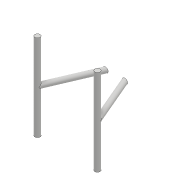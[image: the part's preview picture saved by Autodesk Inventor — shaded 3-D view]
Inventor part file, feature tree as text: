
AUTODESK INVENTOR PART (.ipt)
format: ipt  version: 2017 (Build 210142000, 142)  size: 103,424 bytes
history: native  units: mm
features: other x8, sketch x3, reference x3, extrude x2, revolve x1, mirror x1
ambient origin geometry x8: Origin, YZ Plane, XZ Plane, XY Plane, X Axis, Y Axis, Z Axis, Center Point
bodies: Body1 (feature_tree)
feature tree (18):
  other  "Bryła1"
  other  "Płaszczyzna konstrukcyjna1"
  revolve  "Obrót1"
  extrude  "Wyciągnięcie proste2"  Depth=120.0mm
  other  "Płaszczyzna konstrukcyjna2"
  other  "Płaszczyzna konstrukcyjna3"
  mirror  "Odbij1"
  extrude  "Wyciągnięcie proste5"  Depth=12.0mm
  sketch  "Szkic1"
  reference  "Odniesienie1"
  reference  "Odniesienie2"
  reference  "Odniesienie3"
  sketch  "Szkic3"
  sketch  "Szkic6"
  other  "<userpath>\Desktop\quadrocopter rysunki\zlozenie.iam"
  other  "zlozenie.iam"
  other  "rama:1"
  other  "płyta_pod_lipol:1"
